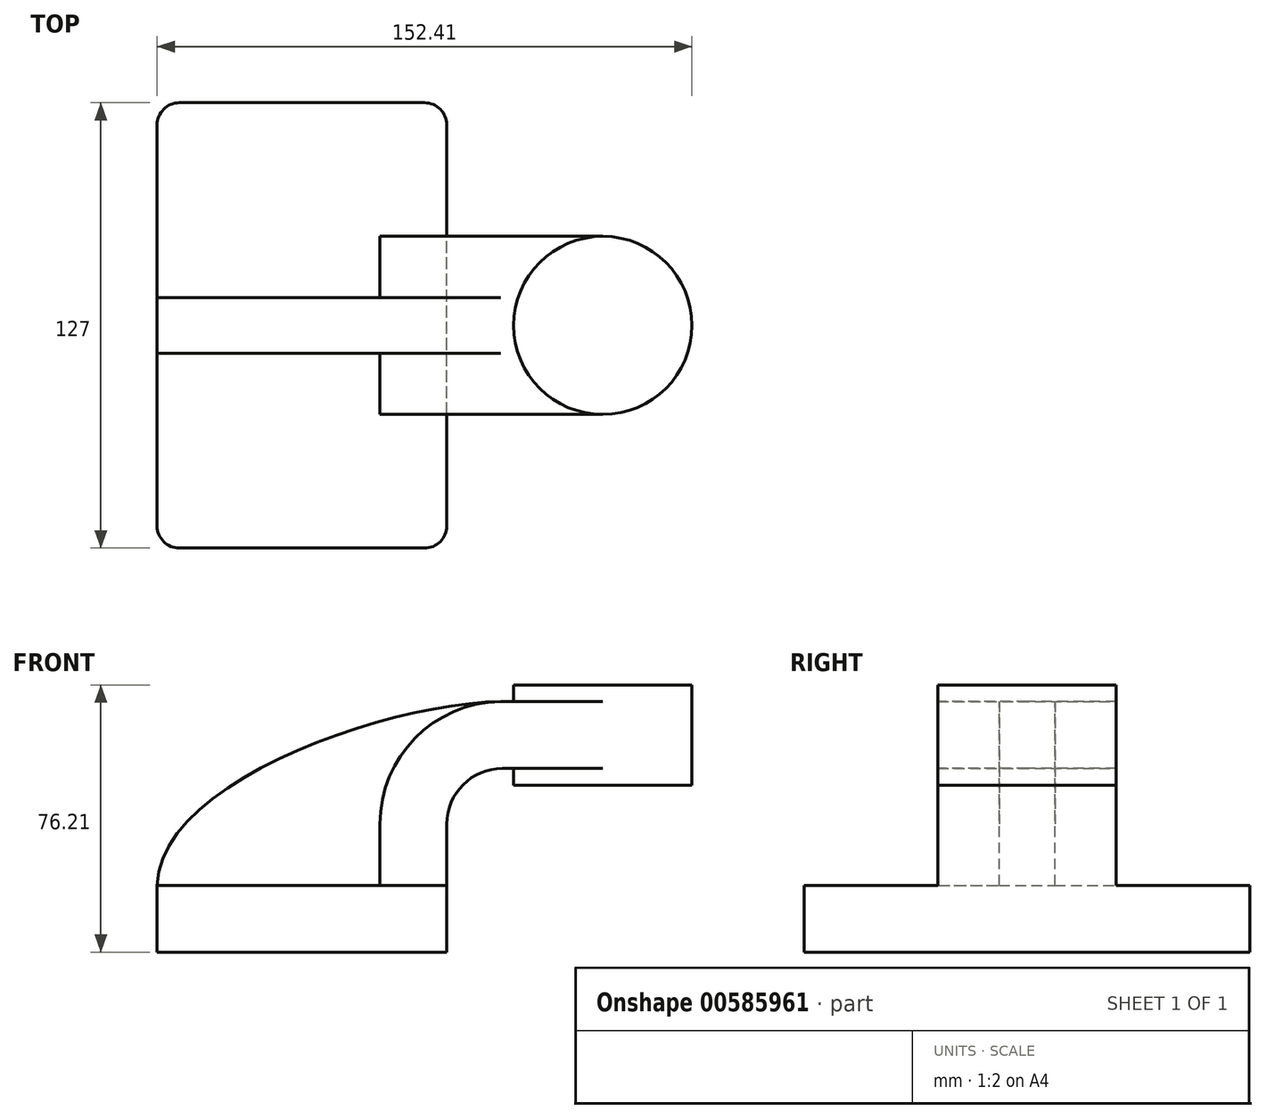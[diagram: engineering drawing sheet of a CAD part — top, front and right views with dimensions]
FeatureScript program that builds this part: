
annotation { "Feature Type Name" : "Feature", "Feature Type Description" : "" }
export const myFeature = defineFeature(function(context is Context, id is Id, definition is map)
    precondition{}
    {
        {
            var Q0;
            Q0=qCreatedBy(makeId("Front.planeOp"),FACE);
            var sketch = newSketch(context, id + "F0", { "sketchPlane" : qUnion([Q0])});
            skLineSegment(sketch, "E0.bottom", {"start": v(41.27, 9.53) * mm, "end": v(-41.27, 9.53) * mm});
            skLineSegment(sketch, "E0.top", {"start": v(41.28, -9.52) * mm, "end": v(-41.27, -9.52) * mm});
            skLineSegment(sketch, "E0.left", {"start": v(41.28, 9.53) * mm, "end": v(41.28, -9.52) * mm});
            skLineSegment(sketch, "E0.right", {"start": v(-41.27, 9.53) * mm, "end": v(-41.27, -9.52) * mm});
            skPoint(sketch, "E0.middle", {"position": v(0, 0) * mm});
            skLineSegment(sketch, "E1.bottom", {"start": v(60.33, 66.68) * mm, "end": v(111.12, 66.68) * mm});
            skLineSegment(sketch, "E1.top", {"start": v(60.33, 38.1) * mm, "end": v(111.12, 38.1) * mm});
            skLineSegment(sketch, "E1.left", {"start": v(60.32, 66.68) * mm, "end": v(60.33, 38.1) * mm});
            skLineSegment(sketch, "E1.right", {"start": v(111.12, 66.68) * mm, "end": v(111.13, 38.1) * mm});
            skPoint(sketch, "E1.middle", {"position": v(85.72, 52.39) * mm});
            skLineSegment(sketch, "E2", {"start": v(41.27, 9.53) * mm, "end": v(41.27, 26.99) * mm});
            skArc(sketch, "E3", {"start": v(41.27, 26.99) * mm, "mid": v(45.92, 38.21) * mm, "end": v(57.15, 42.86) * mm});
            skLineSegment(sketch, "E4", {"start": v(57.15, 42.86) * mm, "end": v(85.72, 42.86) * mm});
            skLineSegment(sketch, "E5.0", {"start": v(57.15, 61.91) * mm, "end": v(85.72, 61.91) * mm});
            skArc(sketch, "E5.1", {"start": v(22.22, 26.99) * mm, "mid": v(32.45, 51.68) * mm, "end": v(57.15, 61.91) * mm});
            skLineSegment(sketch, "E5.2", {"start": v(22.22, 9.53) * mm, "end": v(22.22, 26.99) * mm});
            skLineSegment(sketch, "E6", {"start": v(85.72, 38.1) * mm, "end": v(85.72, 66.68) * mm});
            skFitSpline(sketch, "E7", {"points": [v(-41.28, 9.52) * mm, v(57.15, 61.91) * mm], "startDerivative": vector(2.37, 90.31) * mm, "endDerivative": vector(94.95, 0.37) * mm});
            skSolve(sketch);
        }
        {
            var Q0;
            Q0=makeQuery(id+"F0.imprint","IMPRINT",FACE,{"disambiguationData":[TD([[makeQuery(id+"F0.imprint","IMPRINT",EDGE,{"derivedFrom":sQuery(id+"F0.wireOp",EDGE,"E0.top")}),-1.0]])]});
            extrude(context, id + "F1", {"entities" : qUnion([Q0]), "endBound" : BoundingType.SYMMETRIC, "depth" : 127 * mm, "offsetDistance" : 25.4 * mm});
        }
        {
            var Q0;
            {var subQ1=sQuery(id+"F0.wireOp",EDGE,"E2");Q0=makeQuery(id+"F0.imprint","IMPRINT",FACE,{"disambiguationData":[TD([[makeQuery(id+"F0.imprint","IMPRINT",EDGE,{"derivedFrom":subQ1}),1.0]])]});}
            var Q1;
            {var subQ0=sQuery(id+"F0.wireOp",EDGE,"E5.0");var subQ1=sQuery(id+"F0.wireOp",EDGE,"E1.left");var subQ2=makeQuery(id+"F0.imprint","INTERSECT",VERTEX,{"derivedFrom":[subQ1,subQ0]});Q1=makeQuery(id+"F0.imprint","IMPRINT",FACE,{"disambiguationData":[TD([[makeQuery(id+"F0.imprint","IMPRINT",EDGE,{"disambiguationData":[TD([[subQ2,-1.0]])],"derivedFrom":subQ1}),1.0]])]});}
            extrude(context, id + "F2", {"entities" : qUnion([Q0, Q1]), "operationType" : NewBodyOperationType.ADD, "endBound" : BoundingType.SYMMETRIC, "depth" : 50.8 * mm, "offsetDistance" : 25.4 * mm});
        }
        {
            var Q0;
            {var subQ3=sQuery(id+"F0.wireOp",EDGE,"E5.2");Q0=makeQuery(id+"F0.imprint","IMPRINT",FACE,{"disambiguationData":[TD([[makeQuery(id+"F0.imprint","IMPRINT",EDGE,{"derivedFrom":subQ3}),1.0]])]});}
            extrude(context, id + "F3", {"entities" : qUnion([Q0]), "operationType" : NewBodyOperationType.ADD, "endBound" : BoundingType.SYMMETRIC, "depth" : 15.88 * mm, "offsetDistance" : 25.4 * mm});
        }
        {
            var Q0;
            {var subQ4=sQuery(id+"F0.wireOp",EDGE,"E1.right");Q0=makeQuery(id+"F0.imprint","IMPRINT",FACE,{"disambiguationData":[TD([[makeQuery(id+"F0.imprint","IMPRINT",EDGE,{"derivedFrom":subQ4}),-1.0]])]});}
            var Q1;
            Q1=sQuery(id+"F0.wireOp",EDGE,"E6");
            revolve(context, id + "F4", {"operationType" : NewBodyOperationType.ADD, "entities" : qUnion([Q0]), "axis" : qUnion([Q1]), "revolveType" : RevolveType.FULL});
        }
        {
            var Q0;
            Q0=makeQuery(id+"F1.opExtrude","CAP_EDGE",EDGE,{"disambiguationData":[OSD([sQuery(id+"F0.wireOp",EDGE,"E0.right")])],"isStart":false});
            var Q1;
            Q1=makeQuery(id+"F1.opExtrude","CAP_EDGE",EDGE,{"disambiguationData":[OSD([sQuery(id+"F0.wireOp",EDGE,"E0.right")])],"isStart":true});
            var Q2;
            Q2=makeQuery(id+"F1.opExtrude","CAP_EDGE",EDGE,{"disambiguationData":[OSD([sQuery(id+"F0.wireOp",EDGE,"E0.left")])],"isStart":false});
            var Q3;
            Q3=makeQuery(id+"F1.opExtrude","CAP_EDGE",EDGE,{"disambiguationData":[OSD([sQuery(id+"F0.wireOp",EDGE,"E0.left")])],"isStart":true});
            fillet(context, id + "F5", {"entities" : qUnion([Q0, Q1, Q2, Q3]), "radius" : 6.35 * mm, "tangentPropagation" : true, "allowEdgeOverflow" : false});
        }
    });
